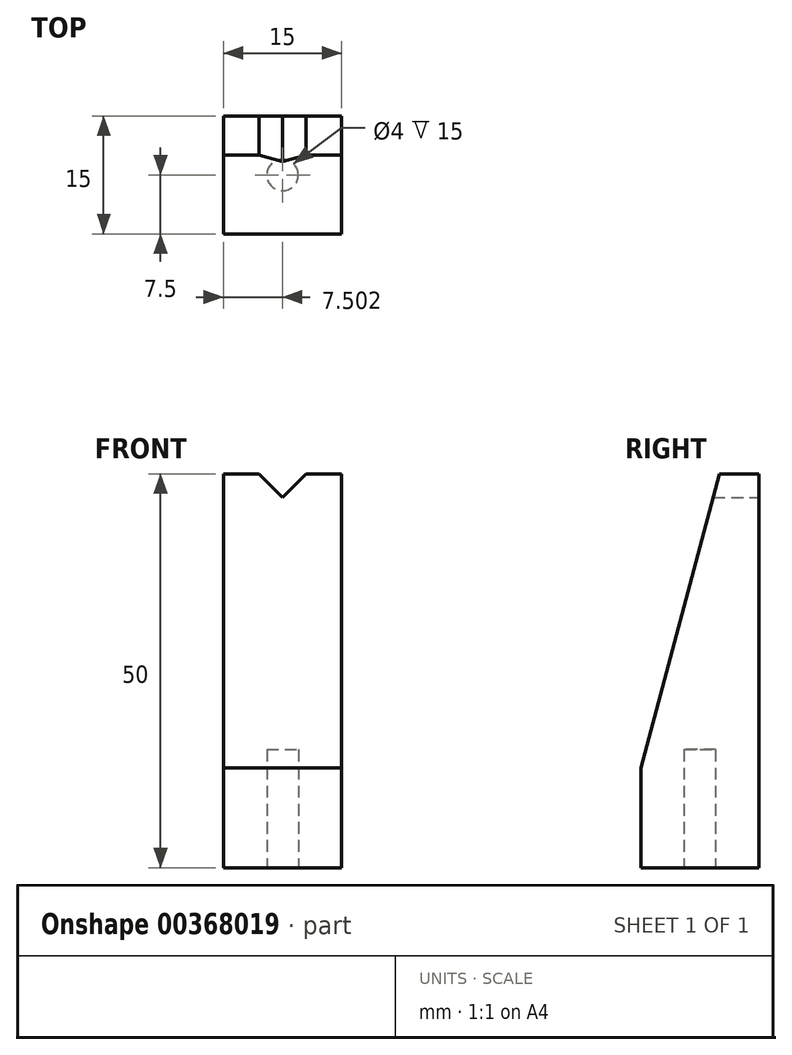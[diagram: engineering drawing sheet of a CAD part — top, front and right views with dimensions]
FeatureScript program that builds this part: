
annotation { "Feature Type Name" : "Feature", "Feature Type Description" : "" }
export const myFeature = defineFeature(function(context is Context, id is Id, definition is map)
    precondition{}
    {
        {
            var Q0;
            Q0=qCreatedBy(makeId("Front.planeOp"),FACE);
            var sketch = newSketch(context, id + "F0", { "sketchPlane" : qUnion([Q0])});
            skLineSegment(sketch, "E0.bottom", {"start": v(-2.7, 40.72) * mm, "end": v(1.8, 40.72) * mm});
            skLineSegment(sketch, "E0.top", {"start": v(-2.7, -9.28) * mm, "end": v(12.3, -9.28) * mm});
            skLineSegment(sketch, "E0.left", {"start": v(-2.7, 40.72) * mm, "end": v(-2.7, -9.28) * mm});
            skLineSegment(sketch, "E0.right", {"start": v(12.3, 40.72) * mm, "end": v(12.3, -9.28) * mm});
            skLineSegment(sketch, "E1", {"start": v(4.8, 48.85) * mm, "end": v(4.8, -9.28) * mm, "construction": true});
            skPoint(sketch, "E1.startSnap0", {"position": v(4.8, 40.72) * mm});
            skLineSegment(sketch, "E2", {"start": v(4.8, 37.72) * mm, "end": v(1.8, 40.72) * mm});
            skLineSegment(sketch, "E3.MirrorCS", {"start": v(4.8, 37.72) * mm, "end": v(7.8, 40.72) * mm});
            skPoint(sketch, "E4.orphan", {"position": v(31.7, 64.62) * mm});
            skPoint(sketch, "E5.orphan", {"position": v(-22.1, 64.62) * mm});
            skLineSegment(sketch, "E6.trimOffspring", {"start": v(7.8, 40.72) * mm, "end": v(12.3, 40.72) * mm});
            skSolve(sketch);
        }
        {
            var Q0;
            Q0=makeQuery(id+"F0.imprint","IMPRINT",FACE,{"disambiguationData":[TD([[makeQuery(id+"F0.imprint","IMPRINT",EDGE,{"derivedFrom":sQuery(id+"F0.wireOp",EDGE,"E0.bottom")}),-1.0]])]});
            extrude(context, id + "F1", {"entities" : qUnion([Q0]), "depth" : 15 * mm});
        }
        {
            var Q0;
            Q0=makeQuery(id+"F1.opExtrude","SWEPT_FACE",FACE,{"disambiguationData":[OSD([sQuery(id+"F0.wireOp",EDGE,"E0.right")])]});
            var sketch = newSketch(context, id + "F2", { "sketchPlane" : qUnion([Q0])});
            skLineSegment(sketch, "E7", {"start": v(-5, 40.72) * mm, "end": v(-15, 3.4) * mm});
            skLineSegment(sketch, "E8", {"start": v(-5, 40.72) * mm, "end": v(0, 40.72) * mm});
            skLineSegment(sketch, "E9", {"start": v(0, 40.72) * mm, "end": v(0, -9.28) * mm});
            skLineSegment(sketch, "E10", {"start": v(0, -9.28) * mm, "end": v(-15, -9.28) * mm});
            skLineSegment(sketch, "E11", {"start": v(-15, -9.28) * mm, "end": v(-15, 3.4) * mm});
            skSolve(sketch);
        }
        {
            var Q0;
            {var subQ0=sQuery(id+"F2.wireOp",EDGE,"E7");Q0=makeQuery(id+"F2.imprint","IMPRINT",FACE,{"disambiguationData":[TD([[makeQuery(id+"F2.imprint","IMPRINT",EDGE,{"derivedFrom":subQ0}),-1.0]])]});}
            extrude(context, id + "F3", {"entities" : qUnion([Q0]), "operationType" : NewBodyOperationType.REMOVE, "oppositeDirection" : true, "depth" : 25 * mm});
        }
        {
            var Q0;
            Q0=makeQuery(id+"F1.opExtrude","SWEPT_FACE",FACE,{"disambiguationData":[OSD([sQuery(id+"F0.wireOp",EDGE,"E0.top")])]});
            var sketch = newSketch(context, id + "F4", { "sketchPlane" : qUnion([Q0])});
            skLineSegment(sketch, "E12", {"start": v(4.8, 15) * mm, "end": v(4.8, 0) * mm, "construction": true});
            skLineSegment(sketch, "E13", {"start": v(12.3, 7.5) * mm, "end": v(-2.7, 7.5) * mm, "construction": true});
            skCircle(sketch, "E14", {"center": v(4.8, 7.5) * mm, "radius": 2 * mm});
            skSolve(sketch);
        }
        {
            var Q0;
            Q0=makeQuery(id+"F4.imprint","IMPRINT",FACE,{"disambiguationData":[TD([[makeQuery(id+"F4.imprint","IMPRINT",EDGE,{"derivedFrom":sQuery(id+"F4.wireOp",EDGE,"E14")}),1.0]])]});
            var Q1;
            Q1=sQuery(id+"F4.wireOp",EDGE,"E14");
            extrude(context, id + "F5", {"entities" : qUnion([Q0]), "operationType" : NewBodyOperationType.REMOVE, "surfaceEntities" : qUnion([Q1]), "oppositeDirection" : true, "depth" : 15 * mm});
        }
    });
